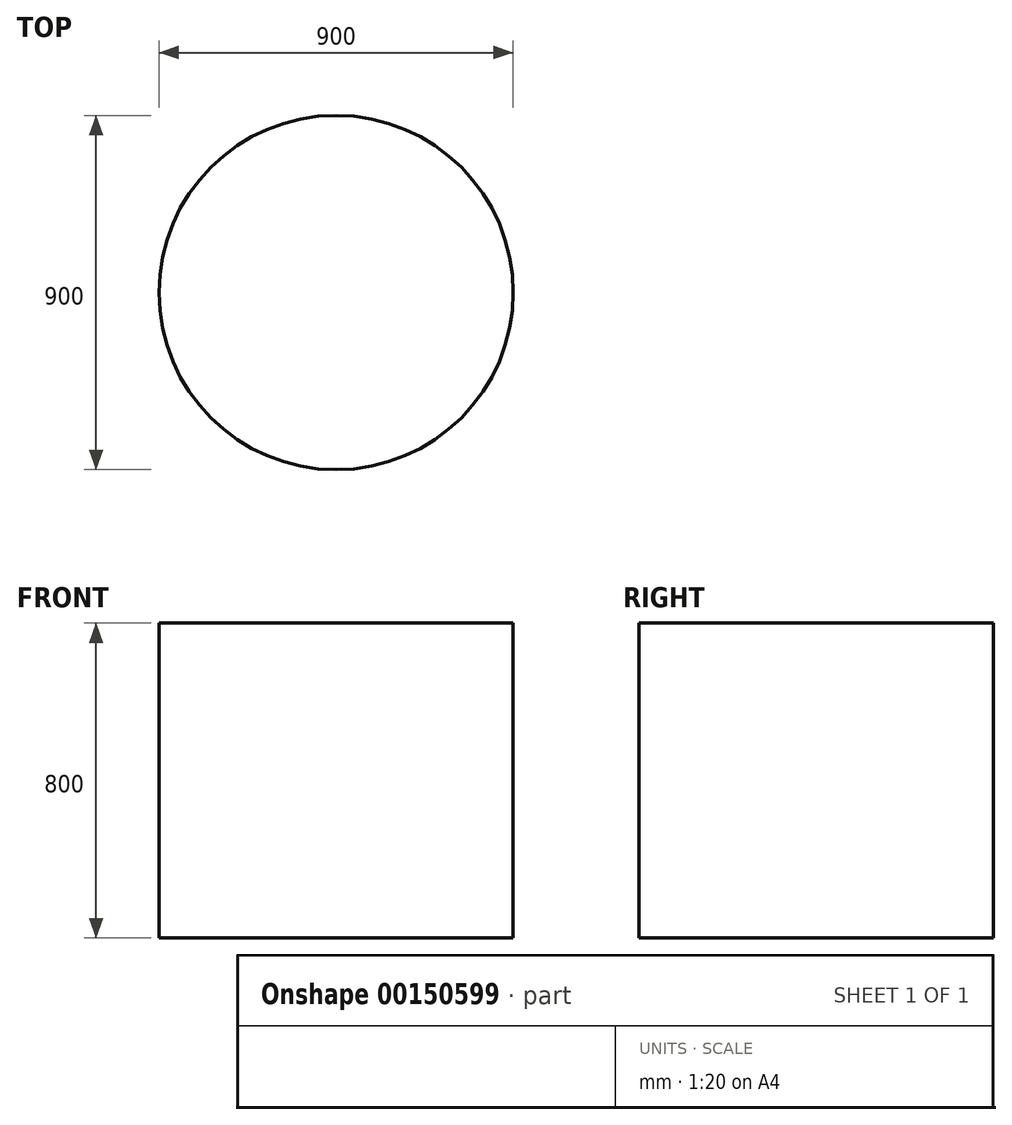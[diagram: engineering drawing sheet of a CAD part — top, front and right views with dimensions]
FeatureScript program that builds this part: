
annotation { "Feature Type Name" : "Feature", "Feature Type Description" : "" }
export const myFeature = defineFeature(function(context is Context, id is Id, definition is map)
    precondition{}
    {
        {
            var Q0;
            Q0=qCreatedBy(makeId("Top.planeOp"),FACE);
            var sketch = newSketch(context, id + "F0", { "sketchPlane" : qUnion([Q0])});
            skCircle(sketch, "E0", {"center": v(0, 0) * mm, "radius": 450 * mm});
            skSolve(sketch);
        }
        {
            var Q0;
            Q0=makeQuery(id+"F0.imprint","IMPRINT",FACE,{"disambiguationData":[TD([[makeQuery(id+"F0.imprint","IMPRINT",EDGE,{"derivedFrom":sQuery(id+"F0.wireOp",EDGE,"E0")}),1.0]])]});
            extrude(context, id + "F1", {"entities" : qUnion([Q0]), "depth" : 800 * mm});
        }
    });
